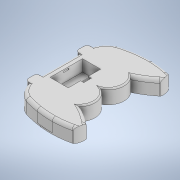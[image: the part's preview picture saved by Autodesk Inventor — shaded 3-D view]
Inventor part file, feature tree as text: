
AUTODESK INVENTOR PART (.ipt)
format: ipt  version: 2022 (Build 260153000, 153)  size: 533,504 bytes
history: native  units: mm
features: sketch x9, extrude x8, fillet x2, chamfer x1
ambient origin geometry x8: Origin, YZ Plane, XZ Plane, XY Plane, X Axis, Y Axis, Z Axis, Center Point
bodies: Solid1 (feature_tree)
feature tree (20):
  sketch  "Sketch1"  dims[d0=35.0mm d1=60.0mm]
  extrude  "Extrusion1"  Depth=60.0mm
  extrude  "Extrusion2"  Depth=25.0mm
  fillet  "Fillet1"  Radius=22.5mm
  extrude  "Extrusion3"  Depth=27.0mm
  fillet  "Fillet2"  Radius=34.0mm
  extrude  "Extrusion4"  Depth=7.5mm
  extrude  "Extrusion5"  Depth=27.0mm
  extrude  "Extrusion6"  Depth=6.0mm
  extrude  "Extrusion7"  Depth=6.5mm
  extrude  "Extrusion8"  Depth=40.0mm TaperAngle=360.0deg
  chamfer  "Chamfer1"  Distance=27.0mm
  sketch  "Sketch2"  dims[d2=17.5mm d3=25.0mm d4=22.5mm]
  sketch  "Sketch4"  dims[d6=25.0mm d7=27.0mm d8=34.0mm]
  sketch  "Sketch5"  dims[d9=27.0mm d10=7.5mm]
  sketch  "Sketch6"  dims[d11=25.0mm d12=27.0mm d13=34.0mm d14=27.0mm]
  sketch  "Sketch7"  dims[d15=6.0mm d16=6.0mm]
  sketch  "Sketch8"  dims[d17=6.0mm d18=6.5mm]
  sketch  "Sketch9"  dims[d22=6.0mm d23=40.0mm d25=360.0deg]
  sketch  "Sketch10"  dims[d27=25.0mm d28=27.0mm d31=40.0mm d32=25.0mm d33=27.0mm d34=5.0mm d35=8.0mm d36=8.0mm d58=40.0mm d60=360.0deg d62=50.0mm d63=2.0mm d64=0.0mm d70=13.425896mm d72=37.3mm d73=4.0mm d74=37.3mm d86=6.5mm d93=0.5mm d95=40.0mm d97=40.0mm d98=20.0mm d99=0.0mm d100=5.0mm d101=10.0mm d102=0.0mm d103=2.0mm d104=25.0mm d105=28.0mm d106=50.0mm d107=10.0mm d108=15.0mm d109=0.0mm d110=2.0mm d111=0.0mm d112=4.0mm d113=4.0mm d115=4.0mm d116=8.0mm d117=2.0mm d118=2.0mm d119=2.0mm d120=0.0mm d121=4.0mm d122=8.0mm d123=2.0mm d124=5.0mm d125=12.0mm d126=2.0mm d127=0.0mm d128=2.5mm d129=2.0mm d130=0.0mm d131=1.0mm d132=2.0mm d133=45.0deg]
